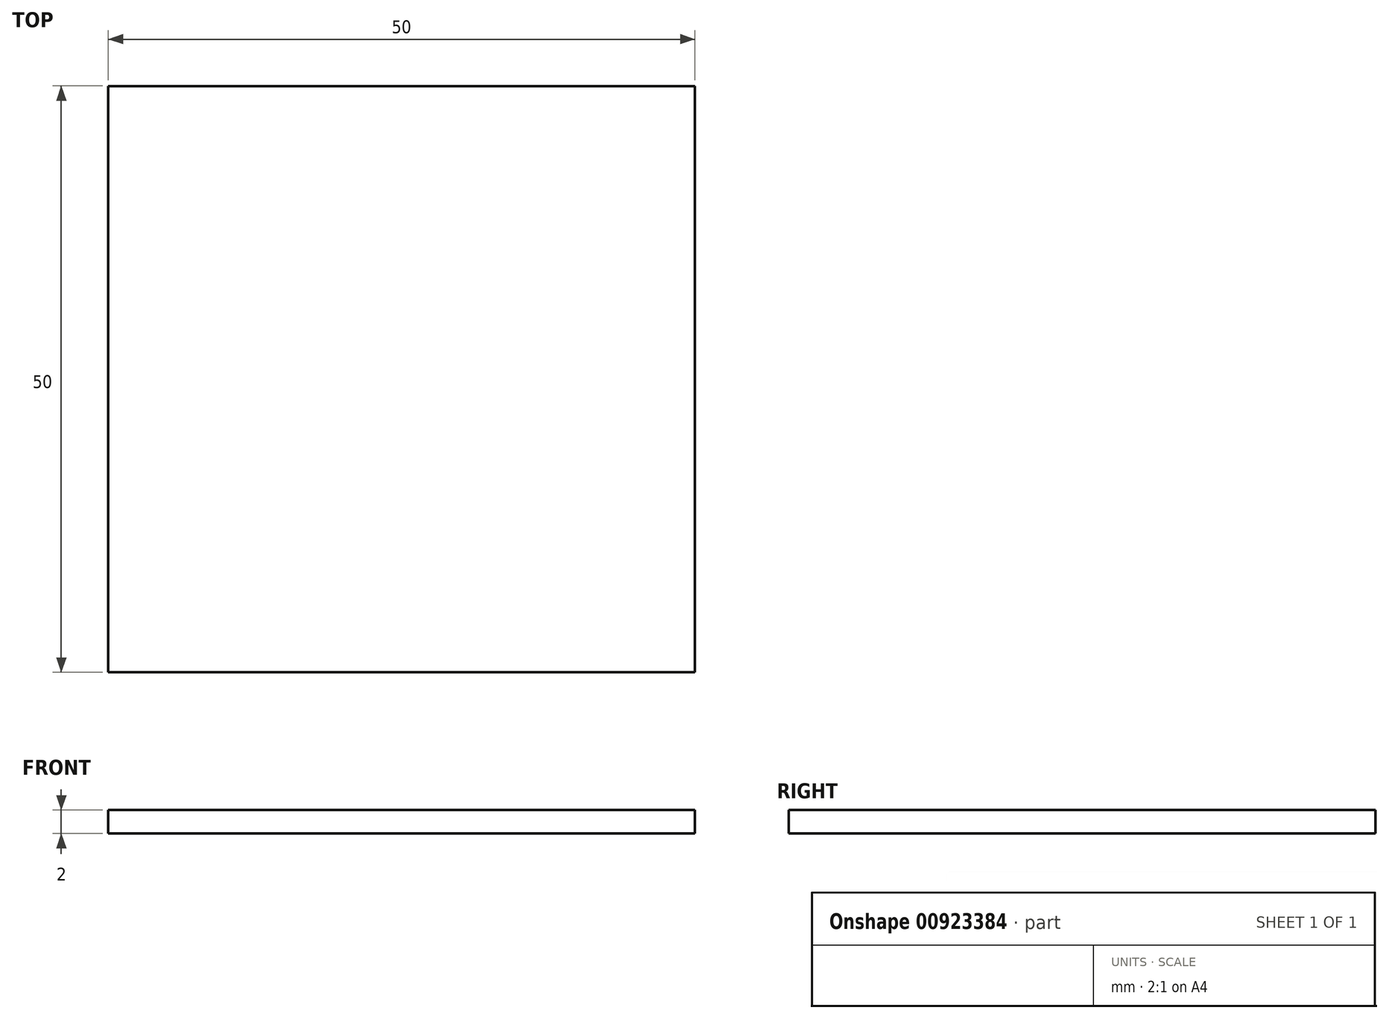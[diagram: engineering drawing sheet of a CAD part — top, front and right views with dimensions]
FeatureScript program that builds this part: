
annotation { "Feature Type Name" : "Feature", "Feature Type Description" : "" }
export const myFeature = defineFeature(function(context is Context, id is Id, definition is map)
    precondition{}
    {
        {
            var Q0;
            Q0=qCreatedBy(makeId("Top.planeOp"),FACE);
            var sketch = newSketch(context, id + "F0", { "sketchPlane" : qUnion([Q0])});
            skLineSegment(sketch, "E0.bottom", {"start": v(22.93, -22.71) * mm, "end": v(-27.07, -22.71) * mm});
            skLineSegment(sketch, "E0.top", {"start": v(22.93, 27.29) * mm, "end": v(-27.07, 27.29) * mm});
            skLineSegment(sketch, "E0.left", {"start": v(22.93, -22.71) * mm, "end": v(22.93, 27.29) * mm});
            skLineSegment(sketch, "E0.right", {"start": v(-27.07, -22.71) * mm, "end": v(-27.07, 27.29) * mm});
            skPoint(sketch, "E0.middle", {"position": v(-2.07, 2.29) * mm});
            skSolve(sketch);
        }
        {
            var Q0;
            Q0=makeQuery(id+"F0.imprint","IMPRINT",FACE,{"disambiguationData":[TD([[makeQuery(id+"F0.imprint","IMPRINT",EDGE,{"derivedFrom":sQuery(id+"F0.wireOp",EDGE,"E0.bottom")}),-1.0]])]});
            extrude(context, id + "F1", {"entities" : qUnion([Q0]), "depth" : 2 * mm, "offsetDistance" : 25.4 * mm});
        }
    });
